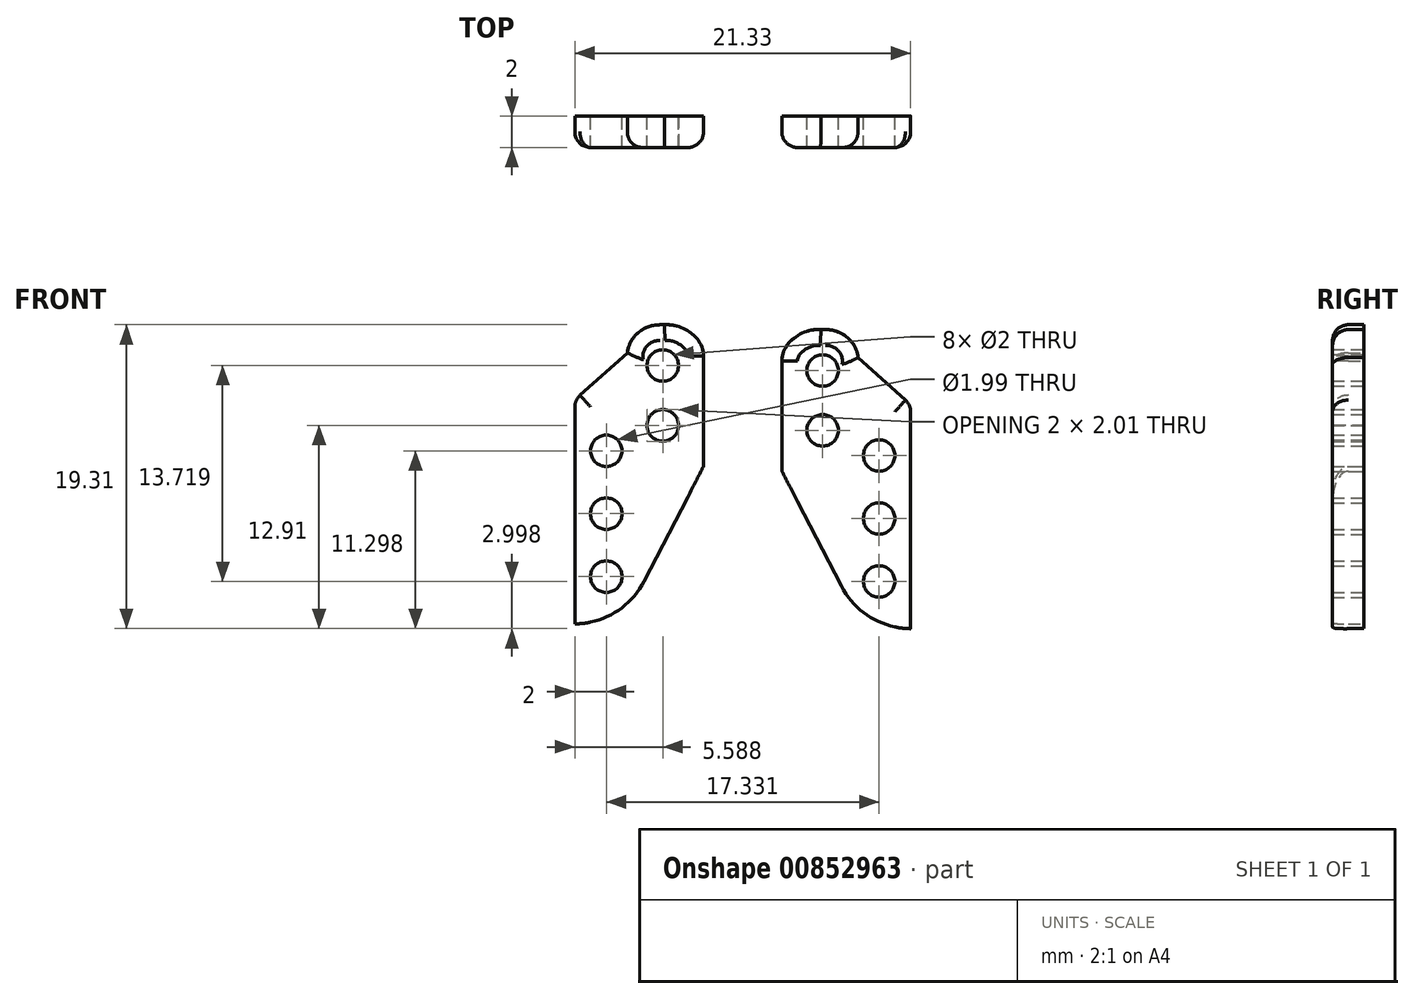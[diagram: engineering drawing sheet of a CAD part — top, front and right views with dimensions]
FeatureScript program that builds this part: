
annotation { "Feature Type Name" : "Feature", "Feature Type Description" : "" }
export const myFeature = defineFeature(function(context is Context, id is Id, definition is map)
    precondition{}
    {
        {
            var Q0;
            Q0=qCreatedBy(makeId("Front.planeOp"),FACE);
            var sketch = newSketch(context, id + "F0", { "sketchPlane" : qUnion([Q0])});
            skLineSegment(sketch, "E0.0.0", {"start": v(5.4, -9.76) * mm, "end": v(5.7, -9.76) * mm});
            skEllipticalArc(sketch, "E0.0.1", {});
            skLineSegment(sketch, "E0.0.5", {"start": v(8.18, -18.76) * mm, "end": v(8.18, -11.76) * mm});
            skFitSpline(sketch, "E0.0.6", {"points": [v(8.18, -11.76) * mm, v(8.18, -11.6) * mm, v(8.15, -11.4) * mm, v(8.05, -11.11) * mm, v(7.92, -10.85) * mm, v(7.7, -10.56) * mm, v(7.36, -10.27) * mm, v(6.98, -10.04) * mm, v(6.44, -9.82) * mm, v(6, -9.76) * mm, v(5.7, -9.76) * mm]});
            skLineSegment(sketch, "E1", {"start": v(0, -14.53) * mm, "end": v(0, -28.76) * mm});
            skLineSegment(sketch, "E2", {"start": v(0, -28.76) * mm, "end": v(3, -28.76) * mm});
            skLineSegment(sketch, "E3", {"start": v(3, -28.76) * mm, "end": v(8.18, -18.76) * mm});
            skLineSegment(sketch, "E4", {"start": v(3, -18.76) * mm, "end": v(3, -28.76) * mm, "construction": true});
            skPoint(sketch, "E5.0", {"position": v(3.17, -13) * mm});
            skPoint(sketch, "E6.0.end.orphan", {"position": v(2.54, -18.76) * mm});
            skCircle(sketch, "E7.0", {"center": v(5.59, -12.34) * mm, "radius": 1 * mm});
            skArc(sketch, "E8.0", {"start": v(4.59, -16.15) * mm, "mid": v(5.6, -15.14) * mm, "end": v(6.59, -16.16) * mm});
            skArc(sketch, "E8.1", {"start": v(4.59, -16.15) * mm, "mid": v(5.58, -17.16) * mm, "end": v(6.59, -16.16) * mm});
            skCircle(sketch, "E9", {"center": v(2, -25.76) * mm, "radius": 1 * mm});
            skCircle(sketch, "E10", {"center": v(2, -21.76) * mm, "radius": 1 * mm});
            skLineSegment(sketch, "E11", {"start": v(3.34, -11.54) * mm, "end": v(0, -14.53) * mm});
            skLineSegment(sketch, "E12", {"start": v(2, -31.48) * mm, "end": v(2, -8.31) * mm, "construction": true});
            skCircle(sketch, "E13", {"center": v(2, -17.76) * mm, "radius": 1 * mm});
            skFitSpline(sketch, "E14.0.6", {"points": [v(8.18, -11.76) * mm, v(8.18, -11.6) * mm, v(8.15, -11.4) * mm, v(8.05, -11.11) * mm, v(7.92, -10.85) * mm, v(7.7, -10.56) * mm, v(7.36, -10.27) * mm, v(6.98, -10.04) * mm, v(6.44, -9.82) * mm, v(6, -9.76) * mm, v(5.7, -9.76) * mm]});
            skLineSegment(sketch, "E15", {"start": v(8.18, 0) * mm, "end": v(8.18, -31.76) * mm, "construction": true});
            skLineSegment(sketch, "E16", {"start": v(13.18, -31.76) * mm, "end": v(13.18, 0) * mm, "construction": true});
            skPoint(sketch, "E17.0.2.end.orphan", {"position": v(6.33, -11.16) * mm});
            skPoint(sketch, "E17.0.3.start.orphan", {"position": v(6.33, -18.16) * mm});
            skLineSegment(sketch, "E18", {"start": v(18.33, -19.06) * mm, "end": v(18.33, -29.06) * mm, "construction": true});
            skLineSegment(sketch, "E19", {"start": v(13.15, -19.06) * mm, "end": v(18.33, -29.06) * mm});
            skLineSegment(sketch, "E20", {"start": v(21.33, -29.06) * mm, "end": v(21.33, -14.84) * mm});
            skLineSegment(sketch, "E21", {"start": v(21.33, -14.84) * mm, "end": v(18, -11.84) * mm});
            skLineSegment(sketch, "E22", {"start": v(21.33, -29.06) * mm, "end": v(18.33, -29.06) * mm});
            skLineSegment(sketch, "E23", {"start": v(19.33, -10.45) * mm, "end": v(19.33, -30.96) * mm, "construction": true});
            skCircle(sketch, "E24", {"center": v(19.33, -26.06) * mm, "radius": 1 * mm});
            skCircle(sketch, "E25", {"center": v(19.33, -22.06) * mm, "radius": 1 * mm});
            skCircle(sketch, "E26", {"center": v(19.33, -18.06) * mm, "radius": 1 * mm});
            skEllipticalArc(sketch, "E27.0", {});
            skFitSpline(sketch, "E28.0", {"points": [v(15.62, -10.06) * mm, v(15.33, -10.06) * mm, v(14.9, -10.13) * mm, v(14.35, -10.34) * mm, v(13.97, -10.57) * mm, v(13.64, -10.86) * mm, v(13.42, -11.15) * mm, v(13.28, -11.42) * mm, v(13.19, -11.7) * mm, v(13.15, -11.91) * mm, v(13.15, -12.06) * mm]});
            skLineSegment(sketch, "E29.0", {"start": v(13.15, -19.06) * mm, "end": v(13.15, -12.06) * mm});
            skCircle(sketch, "E30.0", {"center": v(15.74, -12.66) * mm, "radius": 1 * mm});
            skCircle(sketch, "E31.0", {"center": v(15.74, -16.46) * mm, "radius": 1 * mm});
            skLineSegment(sketch, "E32.0.2", {"start": v(15.93, -10.06) * mm, "end": v(15.62, -10.06) * mm});
            skFitSpline(sketch, "E32.0.3", {"points": [v(15.62, -10.06) * mm, v(15.33, -10.06) * mm, v(14.9, -10.13) * mm, v(14.35, -10.34) * mm, v(13.97, -10.57) * mm, v(13.64, -10.86) * mm, v(13.42, -11.15) * mm, v(13.28, -11.42) * mm, v(13.19, -11.7) * mm, v(13.15, -11.91) * mm, v(13.15, -12.06) * mm]});
            skLineSegment(sketch, "E32.0.4", {"start": v(13.15, -12.06) * mm, "end": v(13.15, -19.06) * mm});
            skPoint(sketch, "E33.0.end.orphan", {"position": v(18.33, -14.78) * mm});
            skPoint(sketch, "E34.0.2.end.orphan", {"position": v(18.79, -19.06) * mm});
            skPoint(sketch, "E35.0.start.orphan", {"position": v(18.33, -19.06) * mm});
            skPoint(sketch, "E36.0.2.end.orphan", {"position": v(5.33, -12.06) * mm});
            skPoint(sketch, "E36.0.3.start.orphan", {"position": v(5.33, -19.06) * mm});
            const initialGuessF0  = {"E0.0.1": [0.005396531449536064, -0.011757296502590178, -1, 0, 0.0020705523608201665, 0.002, 4.71238898038469, 6.172528086005689], "E0.0.1": [0.005396531449536064, -0.011757296502590178, -1, 0, 0.0020705523608201665, 0.002, 4.71238898038469, 6.172528086005689], "E27.0": [0.015934383825107618, -0.012061798229813576, -1, 0, 0.0020705523608201665, 0.002, 3.252249874763688, 4.71238898038469], "E27.0": [0.015934383825107618, -0.012061798229813576, -1, 0, 0.0020705523608201665, 0.002, 3.252249874763688, 4.71238898038469]};
            skSetInitialGuess(sketch, initialGuessF0);
            skSolve(sketch);
        }
        {
            var Q0;
            Q0=makeQuery(id+"F0.imprint","IMPRINT",FACE,{"disambiguationData":[TD([[makeQuery(id+"F0.imprint","IMPRINT",EDGE,{"derivedFrom":sQuery(id+"F0.wireOp",EDGE,"E1")}),1.0]])]});
            var Q1;
            Q1=makeQuery(id+"F0.imprint","IMPRINT",FACE,{"disambiguationData":[TD([[makeQuery(id+"F0.imprint","IMPRINT",EDGE,{"derivedFrom":sQuery(id+"F0.wireOp",EDGE,"E19")}),1.0]])]});
            extrude(context, id + "F1", {"entities" : qUnion([Q0, Q1]), "depth" : 2 * mm, "offsetDistance" : 25 * mm});
        }
        {
            var Q0;
            Q0=makeQuery(id+"F1.opExtrude","CAP_EDGE",EDGE,{"disambiguationData":[OSD([sQuery(id+"F0.wireOp",EDGE,"E0.0.1")])],"isStart":false});
            var Q1;
            Q1=makeQuery(id+"F1.opExtrude","CAP_EDGE",EDGE,{"disambiguationData":[OSD([sQuery(id+"F0.wireOp",EDGE,"E11")])],"isStart":false});
            var Q2;
            Q2=makeQuery(id+"F1.opExtrude","CAP_EDGE",EDGE,{"disambiguationData":[OSD([sQuery(id+"F0.wireOp",EDGE,"E27.0")])],"isStart":false});
            var Q3;
            Q3=makeQuery(id+"F1.opExtrude","CAP_EDGE",EDGE,{"disambiguationData":[OSD([sQuery(id+"F0.wireOp",EDGE,"E21")])],"isStart":false});
            fillet(context, id + "F2", {"entities" : qUnion([Q0, Q1, Q2, Q3]), "radius" : 1 * mm, "tangentPropagation" : true, "allowEdgeOverflow" : false});
        }
        {
            var Q0;
            Q0=makeQuery(id+"F1.opExtrude","SWEPT_EDGE",EDGE,{"disambiguationData":[OSD([sQuery(id+"F0.wireOp",EDGE,"E19"),sQuery(id+"F0.wireOp",EDGE,"E22")])]});
            var Q1;
            Q1=makeQuery(id+"F1.opExtrude","SWEPT_EDGE",EDGE,{"disambiguationData":[OSD([sQuery(id+"F0.wireOp",EDGE,"E2"),sQuery(id+"F0.wireOp",EDGE,"E3")])]});
            fillet(context, id + "F3", {"entities" : qUnion([Q0, Q1]), "radius" : 5 * mm, "tangentPropagation" : true, "allowEdgeOverflow" : false});
        }
        {
            var Q0;
            Q0=makeQuery(id+"F1.opExtrude","CAP_EDGE",EDGE,{"disambiguationData":[OSD([sQuery(id+"F0.wireOp",EDGE,"E20")])],"isStart":false});
            var Q1;
            Q1=makeQuery(id+"F1.opExtrude","CAP_EDGE",EDGE,{"disambiguationData":[OSD([sQuery(id+"F0.wireOp",EDGE,"E1")])],"isStart":false});
            fillet(context, id + "F4", {"entities" : qUnion([Q0, Q1]), "radius" : 1 * mm, "tangentPropagation" : true, "allowEdgeOverflow" : false});
        }
    });
